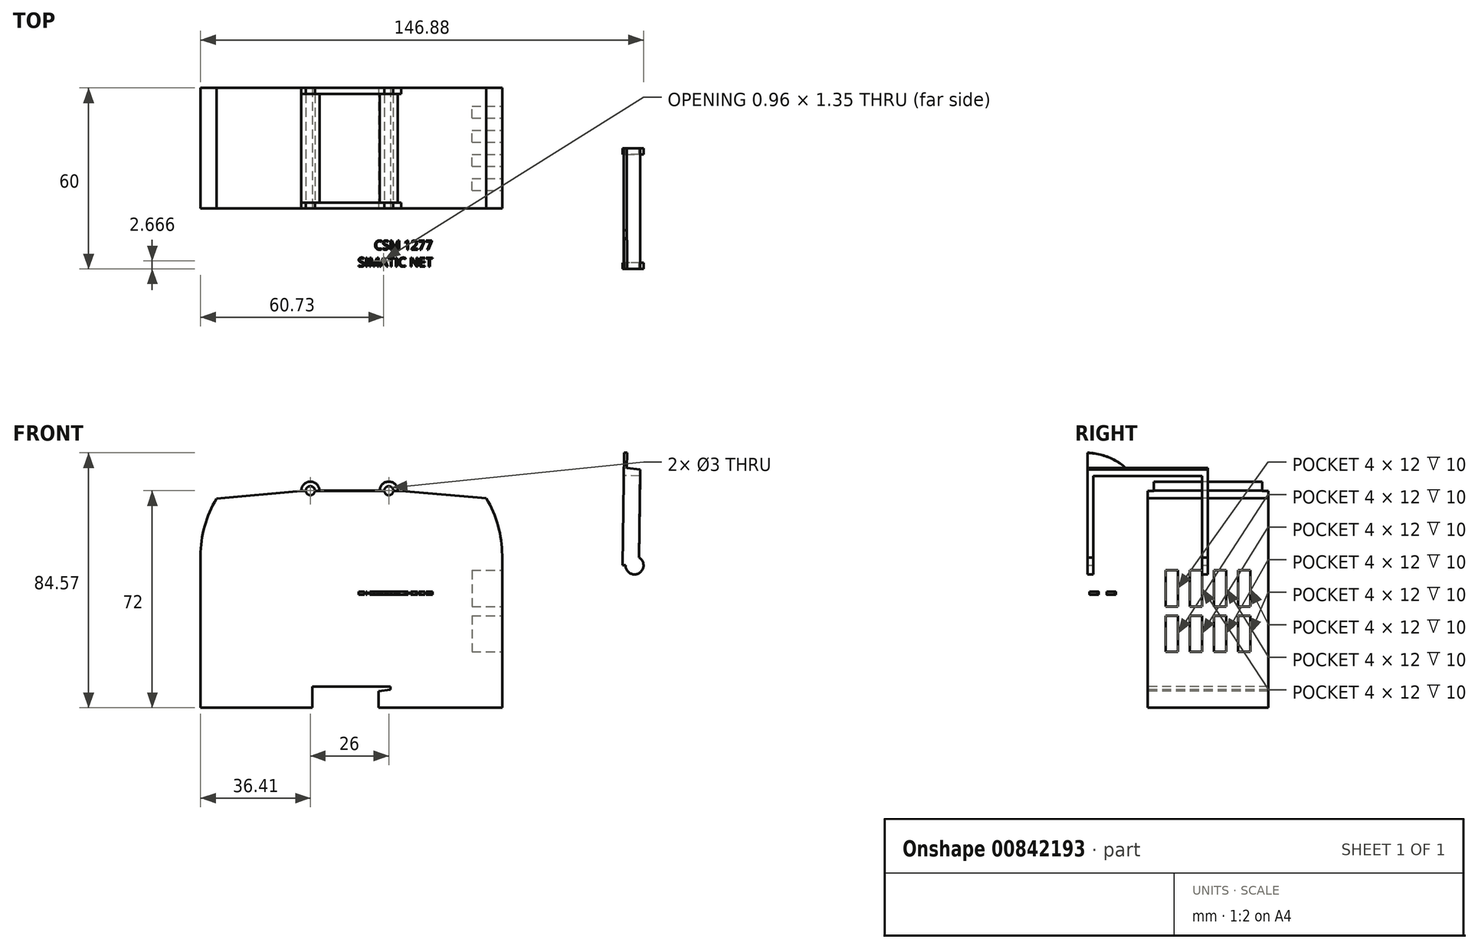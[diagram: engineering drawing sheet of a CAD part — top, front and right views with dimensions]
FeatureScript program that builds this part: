
annotation { "Feature Type Name" : "Feature", "Feature Type Description" : "" }
export const myFeature = defineFeature(function(context is Context, id is Id, definition is map)
    precondition{}
    {
        {
            var Q0;
            Q0=qCreatedBy(makeId("Front.planeOp"),FACE);
            var sketch = newSketch(context, id + "F0", { "sketchPlane" : qUnion([Q0])});
            skLineSegment(sketch, "E0.bottom", {"start": v(50, -37.5) * mm, "end": v(-50, -37.5) * mm});
            skLineSegment(sketch, "E0.top", {"start": v(50, 37.5) * mm, "end": v(-50, 37.5) * mm});
            skLineSegment(sketch, "E0.left", {"start": v(50, -37.5) * mm, "end": v(50, 37.5) * mm});
            skLineSegment(sketch, "E0.right", {"start": v(-50, -37.5) * mm, "end": v(-50, 37.5) * mm});
            skPoint(sketch, "E0.middle", {"position": v(0, 0) * mm});
            skSolve(sketch);
        }
        {
            var Q0;
            Q0=makeQuery(id+"F0.imprint","IMPRINT",FACE,{"disambiguationData":[TD([[makeQuery(id+"F0.imprint","IMPRINT",EDGE,{"derivedFrom":sQuery(id+"F0.wireOp",EDGE,"E0.bottom")}),-1.0]])]});
            extrude(context, id + "F1", {"entities" : qUnion([Q0]), "endBound" : BoundingType.SYMMETRIC, "depth" : 40 * mm, "offsetDistance" : 25 * mm});
        }
        {
            var Q0;
            Q0=makeQuery(id+"F1.opExtrude","CAP_FACE",FACE,{"disambiguationData":[OSD([sQuery(id+"F0.wireOp",EDGE,"E0.bottom"),sQuery(id+"F0.wireOp",EDGE,"E0.top"),sQuery(id+"F0.wireOp",EDGE,"E0.left"),sQuery(id+"F0.wireOp",EDGE,"E0.right")])],"isStart":false});
            var sketch = newSketch(context, id + "F2", { "sketchPlane" : qUnion([Q0])});
            skCircle(sketch, "E1", {"center": v(12.41, 34.5) * mm, "radius": 3 * mm});
            skCircle(sketch, "E2", {"center": v(-13.59, 34.5) * mm, "radius": 3 * mm});
            skLineSegment(sketch, "E3", {"start": v(9.41, 34.5) * mm, "end": v(15.41, 34.5) * mm});
            skLineSegment(sketch, "E4", {"start": v(-10.59, 34.5) * mm, "end": v(-16.59, 34.5) * mm});
            skLineSegment(sketch, "E5", {"start": v(15.41, 34.5) * mm, "end": v(50, 31.5) * mm});
            skLineSegment(sketch, "E6.MirrorCS", {"start": v(-15.09, 34.5) * mm, "end": v(-50.09, 31.36) * mm});
            skLineSegment(sketch, "E7", {"start": v(-10.59, 34.5) * mm, "end": v(9.41, 34.5) * mm});
            skCircle(sketch, "E8", {"center": v(-13.59, 34.5) * mm, "radius": 1.5 * mm});
            skCircle(sketch, "E9", {"center": v(12.41, 34.5) * mm, "radius": 1.5 * mm});
            skLineSegment(sketch, "E10", {"start": v(-50.09, 31.36) * mm, "end": v(-50, 37.5) * mm});
            skLineSegment(sketch, "E11", {"start": v(-50, 37.5) * mm, "end": v(50, 37.5) * mm});
            skLineSegment(sketch, "E12", {"start": v(50, 37.5) * mm, "end": v(50, 31.5) * mm});
            skSolve(sketch);
        }
        {
            var Q0;
            {var subQ3=sQuery(id+"F2.wireOp",EDGE,"E2");var subQ8=makeQuery(id+"F2.imprint","INTERSECT",VERTEX,{"derivedFrom":[subQ3,sQuery(id+"F2.wireOp",EDGE,"E4")]});Q0=makeQuery(id+"F2.imprint","IMPRINT",FACE,{"disambiguationData":[TD([[makeQuery(id+"F2.imprint","IMPRINT",EDGE,{"disambiguationData":[TD([[subQ8,1.0]])],"derivedFrom":subQ3}),-1.0]])]});}
            var Q1;
            {var subQ0=sQuery(id+"F2.wireOp",EDGE,"E7");Q1=makeQuery(id+"F2.imprint","IMPRINT",FACE,{"disambiguationData":[TD([[makeQuery(id+"F2.imprint","IMPRINT",EDGE,{"derivedFrom":subQ0}),1.0]])]});}
            var Q2;
            {var subQ0=sQuery(id+"F2.wireOp",EDGE,"E5");Q2=makeQuery(id+"F2.imprint","IMPRINT",FACE,{"disambiguationData":[TD([[makeQuery(id+"F2.imprint","IMPRINT",EDGE,{"derivedFrom":subQ0}),1.0]])]});}
            var Q3;
            {var subQ0=sQuery(id+"F2.wireOp",EDGE,"E8");var subQ1=sQuery(id+"F2.wireOp",EDGE,"E4");var subQ3=makeQuery(id+"F2.imprint","INTERSECT",VERTEX,{"derivedFrom":[subQ1,subQ0]});Q3=makeQuery(id+"F2.imprint","IMPRINT",FACE,{"disambiguationData":[TD([[makeQuery(id+"F2.imprint","IMPRINT",EDGE,{"disambiguationData":[TD([[subQ3,-1.0]])],"derivedFrom":subQ1}),-1.0]])]});}
            var Q4;
            {var subQ0=sQuery(id+"F2.wireOp",EDGE,"E8");var subQ1=sQuery(id+"F2.wireOp",EDGE,"E4");var subQ3=makeQuery(id+"F2.imprint","INTERSECT",VERTEX,{"derivedFrom":[subQ1,subQ0]});Q4=makeQuery(id+"F2.imprint","IMPRINT",FACE,{"disambiguationData":[TD([[makeQuery(id+"F2.imprint","IMPRINT",EDGE,{"disambiguationData":[TD([[subQ3,-1.0]])],"derivedFrom":subQ1}),1.0]])]});}
            var Q5;
            {var subQ0=sQuery(id+"F2.wireOp",EDGE,"E9");var subQ1=sQuery(id+"F2.wireOp",EDGE,"E3");var subQ2=makeQuery(id+"F2.imprint","INTERSECT",VERTEX,{"disambiguationData":[OD(0.0)],"derivedFrom":[subQ1,subQ0]});Q5=makeQuery(id+"F2.imprint","IMPRINT",FACE,{"disambiguationData":[TD([[makeQuery(id+"F2.imprint","IMPRINT",EDGE,{"disambiguationData":[TD([[subQ2,-1.0]])],"derivedFrom":subQ1}),1.0]])]});}
            var Q6;
            {var subQ0=sQuery(id+"F2.wireOp",EDGE,"E9");var subQ1=sQuery(id+"F2.wireOp",EDGE,"E3");var subQ2=makeQuery(id+"F2.imprint","INTERSECT",VERTEX,{"disambiguationData":[OD(0.0)],"derivedFrom":[subQ1,subQ0]});Q6=makeQuery(id+"F2.imprint","IMPRINT",FACE,{"disambiguationData":[TD([[makeQuery(id+"F2.imprint","IMPRINT",EDGE,{"disambiguationData":[TD([[subQ2,-1.0]])],"derivedFrom":subQ1}),-1.0]])]});}
            extrude(context, id + "F3", {"entities" : qUnion([Q0, Q1, Q2, Q3, Q4, Q5, Q6]), "operationType" : NewBodyOperationType.REMOVE, "oppositeDirection" : true, "depth" : 40 * mm, "offsetDistance" : 25 * mm});
        }
        {
            var Q0;
            Q0=makeQuery(id+"F1.opExtrude","CAP_FACE",FACE,{"disambiguationData":[OSD([sQuery(id+"F0.wireOp",EDGE,"E0.bottom"),sQuery(id+"F0.wireOp",EDGE,"E0.top"),sQuery(id+"F0.wireOp",EDGE,"E0.left"),sQuery(id+"F0.wireOp",EDGE,"E0.right")])],"isStart":false});
            var sketch = newSketch(context, id + "F4", { "sketchPlane" : qUnion([Q0])});
            skArc(sketch, "E13", {"start": v(-44.71, 31.84) * mm, "mid": v(-48.66, 22.65) * mm, "end": v(-50, 12.74) * mm});
            skArc(sketch, "E14", {"start": v(50, 12.74) * mm, "mid": v(48.68, 22.71) * mm, "end": v(44.71, 31.96) * mm});
            skSolve(sketch);
        }
        {
            var Q0;
            {var subQ0=sQuery(id+"F4.wireOp",EDGE,"E13");var subQ1=makeQuery(id+"F3.boolean.opBoolean","COPY",EDGE,{"derivedFrom":makeQuery(id+"F3.opExtrude","CAP_EDGE",EDGE,{"disambiguationData":[OSD([sQuery(id+"F2.wireOp",EDGE,"E6.MirrorCS")])],"isStart":true})});var subQ2=makeQuery(id+"F4.imprint","INTERSECT",VERTEX,{"derivedFrom":[subQ1,subQ0]});Q0=makeQuery(id+"F4.imprint","IMPRINT",FACE,{"disambiguationData":[TD([[makeQuery(id+"F4.imprint","IMPRINT",EDGE,{"disambiguationData":[TD([[subQ2,-1.0]])],"derivedFrom":subQ0}),-1.0]])]});}
            var Q1;
            {var subQ0=sQuery(id+"F4.wireOp",EDGE,"E14");var subQ1=makeQuery(id+"F3.boolean.opBoolean","COPY",EDGE,{"derivedFrom":makeQuery(id+"F3.opExtrude","CAP_EDGE",EDGE,{"disambiguationData":[OSD([sQuery(id+"F2.wireOp",EDGE,"E5")])],"isStart":true})});var subQ2=makeQuery(id+"F4.imprint","INTERSECT",VERTEX,{"derivedFrom":[subQ1,subQ0]});Q1=makeQuery(id+"F4.imprint","IMPRINT",FACE,{"disambiguationData":[TD([[makeQuery(id+"F4.imprint","IMPRINT",EDGE,{"disambiguationData":[TD([[subQ2,1.0]])],"derivedFrom":subQ0}),-1.0]])]});}
            extrude(context, id + "F5", {"entities" : qUnion([Q0, Q1]), "operationType" : NewBodyOperationType.REMOVE, "oppositeDirection" : true, "depth" : 40 * mm, "offsetDistance" : 25 * mm});
        }
        {
            var Q0;
            Q0=makeQuery(id+"F1.opExtrude","SWEPT_FACE",FACE,{"disambiguationData":[OSD([sQuery(id+"F0.wireOp",EDGE,"E0.left")])]});
            var sketch = newSketch(context, id + "F6", { "sketchPlane" : qUnion([Q0])});
            skLineSegment(sketch, "E15.bottom", {"start": v(-14, 8.06) * mm, "end": v(-10, 8.06) * mm});
            skLineSegment(sketch, "E15.top", {"start": v(-14, -3.94) * mm, "end": v(-10, -3.94) * mm});
            skLineSegment(sketch, "E15.left", {"start": v(-14, 8.06) * mm, "end": v(-14, -3.94) * mm});
            skLineSegment(sketch, "E15.right", {"start": v(-10, 8.06) * mm, "end": v(-10, -3.94) * mm});
            skLineSegment(sketch, "E16.0.1.0", {"start": v(-14, -6.94) * mm, "end": v(-10, -6.94) * mm});
            skLineSegment(sketch, "E16.0.1.1", {"start": v(-10, -6.94) * mm, "end": v(-10, -18.94) * mm});
            skLineSegment(sketch, "E16.0.1.2", {"start": v(-14, -6.94) * mm, "end": v(-14, -18.94) * mm});
            skLineSegment(sketch, "E16.0.1.3", {"start": v(-14, -18.94) * mm, "end": v(-10, -18.94) * mm});
            skLineSegment(sketch, "E16.1.0.0", {"start": v(-6, 8.06) * mm, "end": v(-2, 8.06) * mm});
            skLineSegment(sketch, "E16.1.0.1", {"start": v(-2, 8.06) * mm, "end": v(-2, -3.94) * mm});
            skLineSegment(sketch, "E16.1.0.2", {"start": v(-6, 8.06) * mm, "end": v(-6, -3.94) * mm});
            skLineSegment(sketch, "E16.1.0.3", {"start": v(-6, -3.94) * mm, "end": v(-2, -3.94) * mm});
            skLineSegment(sketch, "E16.1.1.0", {"start": v(-6, -6.94) * mm, "end": v(-2, -6.94) * mm});
            skLineSegment(sketch, "E16.1.1.1", {"start": v(-2, -6.94) * mm, "end": v(-2, -18.94) * mm});
            skLineSegment(sketch, "E16.1.1.2", {"start": v(-6, -6.94) * mm, "end": v(-6, -18.94) * mm});
            skLineSegment(sketch, "E16.1.1.3", {"start": v(-6, -18.94) * mm, "end": v(-2, -18.94) * mm});
            skLineSegment(sketch, "E16.2.0.0", {"start": v(2, 8.06) * mm, "end": v(6, 8.06) * mm});
            skLineSegment(sketch, "E16.2.0.1", {"start": v(6, 8.06) * mm, "end": v(6, -3.94) * mm});
            skLineSegment(sketch, "E16.2.0.2", {"start": v(2, 8.06) * mm, "end": v(2, -3.94) * mm});
            skLineSegment(sketch, "E16.2.0.3", {"start": v(2, -3.94) * mm, "end": v(6, -3.94) * mm});
            skLineSegment(sketch, "E16.2.1.0", {"start": v(2, -6.94) * mm, "end": v(6, -6.94) * mm});
            skLineSegment(sketch, "E16.2.1.1", {"start": v(6, -6.94) * mm, "end": v(6, -18.94) * mm});
            skLineSegment(sketch, "E16.2.1.2", {"start": v(2, -6.94) * mm, "end": v(2, -18.94) * mm});
            skLineSegment(sketch, "E16.2.1.3", {"start": v(2, -18.94) * mm, "end": v(6, -18.94) * mm});
            skLineSegment(sketch, "E16.3.0.0", {"start": v(10, 8.06) * mm, "end": v(14, 8.06) * mm});
            skLineSegment(sketch, "E16.3.0.1", {"start": v(14, 8.06) * mm, "end": v(14, -3.94) * mm});
            skLineSegment(sketch, "E16.3.0.2", {"start": v(10, 8.06) * mm, "end": v(10, -3.94) * mm});
            skLineSegment(sketch, "E16.3.0.3", {"start": v(10, -3.94) * mm, "end": v(14, -3.94) * mm});
            skLineSegment(sketch, "E16.3.1.0", {"start": v(10, -6.94) * mm, "end": v(14, -6.94) * mm});
            skLineSegment(sketch, "E16.3.1.1", {"start": v(14, -6.94) * mm, "end": v(14, -18.94) * mm});
            skLineSegment(sketch, "E16.3.1.2", {"start": v(10, -6.94) * mm, "end": v(10, -18.94) * mm});
            skLineSegment(sketch, "E16.3.1.3", {"start": v(10, -18.94) * mm, "end": v(14, -18.94) * mm});
            skLineSegment(sketch, "E16.direction1", {"start": v(-14, 8.06) * mm, "end": v(-6, 8.06) * mm, "construction": true});
            skLineSegment(sketch, "E16.direction2", {"start": v(-14, 8.06) * mm, "end": v(-14, -6.94) * mm, "construction": true});
            skSolve(sketch);
        }
        {
            var Q0;
            Q0=makeQuery(id+"F6.imprint","IMPRINT",FACE,{"disambiguationData":[TD([[makeQuery(id+"F6.imprint","IMPRINT",EDGE,{"derivedFrom":sQuery(id+"F6.wireOp",EDGE,"E15.bottom")}),-1.0]])]});
            var Q1;
            Q1=makeQuery(id+"F6.imprint","IMPRINT",FACE,{"disambiguationData":[TD([[makeQuery(id+"F6.imprint","IMPRINT",EDGE,{"derivedFrom":sQuery(id+"F6.wireOp",EDGE,"E16.1.0.0")}),-1.0]])]});
            var Q2;
            Q2=makeQuery(id+"F6.imprint","IMPRINT",FACE,{"disambiguationData":[TD([[makeQuery(id+"F6.imprint","IMPRINT",EDGE,{"derivedFrom":sQuery(id+"F6.wireOp",EDGE,"E16.2.0.0")}),-1.0]])]});
            var Q3;
            Q3=makeQuery(id+"F6.imprint","IMPRINT",FACE,{"disambiguationData":[TD([[makeQuery(id+"F6.imprint","IMPRINT",EDGE,{"derivedFrom":sQuery(id+"F6.wireOp",EDGE,"E16.3.0.0")}),-1.0]])]});
            var Q4;
            Q4=makeQuery(id+"F6.imprint","IMPRINT",FACE,{"disambiguationData":[TD([[makeQuery(id+"F6.imprint","IMPRINT",EDGE,{"derivedFrom":sQuery(id+"F6.wireOp",EDGE,"E16.3.1.0")}),-1.0]])]});
            var Q5;
            Q5=makeQuery(id+"F6.imprint","IMPRINT",FACE,{"disambiguationData":[TD([[makeQuery(id+"F6.imprint","IMPRINT",EDGE,{"derivedFrom":sQuery(id+"F6.wireOp",EDGE,"E16.2.1.0")}),-1.0]])]});
            var Q6;
            Q6=makeQuery(id+"F6.imprint","IMPRINT",FACE,{"disambiguationData":[TD([[makeQuery(id+"F6.imprint","IMPRINT",EDGE,{"derivedFrom":sQuery(id+"F6.wireOp",EDGE,"E16.1.1.0")}),-1.0]])]});
            var Q7;
            Q7=makeQuery(id+"F6.imprint","IMPRINT",FACE,{"disambiguationData":[TD([[makeQuery(id+"F6.imprint","IMPRINT",EDGE,{"derivedFrom":sQuery(id+"F6.wireOp",EDGE,"E16.0.1.0")}),-1.0]])]});
            extrude(context, id + "F7", {"entities" : qUnion([Q0, Q1, Q2, Q3, Q4, Q5, Q6, Q7]), "operationType" : NewBodyOperationType.REMOVE, "oppositeDirection" : true, "depth" : 10 * mm, "offsetDistance" : 25 * mm});
        }
        {
            var Q0;
            Q0=makeQuery(id+"F1.opExtrude","SWEPT_FACE",FACE,{"disambiguationData":[OSD([sQuery(id+"F0.wireOp",EDGE,"E0.right")])]});
            var sketch = newSketch(context, id + "F8", { "sketchPlane" : qUnion([Q0])});
            skLineSegment(sketch, "E17", {"start": v(-20.02, 34.4) * mm, "end": v(-18.02, 34.4) * mm});
            skLineSegment(sketch, "E18", {"start": v(-18.02, 34.4) * mm, "end": v(-18.02, 38.84) * mm});
            skLineSegment(sketch, "E19", {"start": v(-18.02, 38.84) * mm, "end": v(-20.02, 38.84) * mm});
            skLineSegment(sketch, "E20", {"start": v(-20.02, 38.84) * mm, "end": v(-20.02, 34.4) * mm});
            skLineSegment(sketch, "E21.MirrorCS", {"start": v(18.02, 34.4) * mm, "end": v(18.02, 38.84) * mm});
            skLineSegment(sketch, "E22.MirrorCS", {"start": v(18.02, 38.84) * mm, "end": v(20.02, 38.84) * mm});
            skLineSegment(sketch, "E23.MirrorCS", {"start": v(20.02, 38.84) * mm, "end": v(20.02, 34.4) * mm});
            skLineSegment(sketch, "E24.MirrorCS", {"start": v(20.02, 34.4) * mm, "end": v(18.02, 34.4) * mm});
            skSolve(sketch);
        }
        {
            var Q0;
            Q0=makeQuery(id+"F8.imprint","IMPRINT",FACE,{"disambiguationData":[TD([[makeQuery(id+"F8.imprint","IMPRINT",EDGE,{"derivedFrom":sQuery(id+"F8.wireOp",EDGE,"E17")}),1.0]])]});
            var Q1;
            Q1=makeQuery(id+"F8.imprint","IMPRINT",FACE,{"disambiguationData":[TD([[makeQuery(id+"F8.imprint","IMPRINT",EDGE,{"derivedFrom":sQuery(id+"F8.wireOp",EDGE,"E21.MirrorCS")}),-1.0]])]});
            extrude(context, id + "F9", {"entities" : qUnion([Q0, Q1]), "operationType" : NewBodyOperationType.REMOVE, "oppositeDirection" : true, "depth" : 100 * mm, "offsetDistance" : 25 * mm});
        }
        {
            var Q0;
            Q0=qCreatedBy(makeId("Top.planeOp"),FACE);
            var sketch = newSketch(context, id + "F10", { "sketchPlane" : qUnion([Q0])});
            skText(sketch, "E25", { "text": "     CSM 1277\nSIMATIC NET", "fontName": "OpenSans-Regular.ttf"});
            const initialGuessF10  = {"E25": [0.0022, -0.0336, 1, 0, 0.003]};
            skSetInitialGuess(sketch, initialGuessF10);
            skSolve(sketch);
        }
        {
            var Q0;
            Q0 = qSketchRegion(id + "F10", true);
            extrude(context, id + "F11", {"entities" : qUnion([Q0]), "depth" : 1 * mm, "offsetDistance" : 25 * mm});
        }
        {
            var Q0;
            Q0=qCreatedBy(makeId("Front.planeOp"),FACE);
            var sketch = newSketch(context, id + "F12", { "sketchPlane" : qUnion([Q0])});
            skLineSegment(sketch, "E26", {"start": v(95.79, 41.48) * mm, "end": v(95.44, 12.24) * mm});
            skLineSegment(sketch, "E27", {"start": v(91.35, 42.05) * mm, "end": v(95.79, 41.48) * mm});
            skCircle(sketch, "E28", {"center": v(93.88, 9.72) * mm, "radius": 3 * mm});
            skLineSegment(sketch, "E29", {"start": v(90.88, 9.76) * mm, "end": v(91.35, 42.05) * mm});
            skSolve(sketch);
        }
        {
            var Q0;
            {var subQ0=sQuery(id+"F12.wireOp",EDGE,"E27");Q0=makeQuery(id+"F12.imprint","IMPRINT",FACE,{"disambiguationData":[TD([[makeQuery(id+"F12.imprint","IMPRINT",EDGE,{"derivedFrom":subQ0}),-1.0]])]});}
            var Q1;
            {var subQ0=sQuery(id+"F12.wireOp",EDGE,"E28");var subQ1=makeQuery(id+"F12.imprint","INTERSECT",VERTEX,{"derivedFrom":[subQ0,sQuery(id+"F12.wireOp",EDGE,"E29")]});Q1=makeQuery(id+"F12.imprint","IMPRINT",FACE,{"disambiguationData":[TD([[makeQuery(id+"F12.imprint","IMPRINT",EDGE,{"disambiguationData":[TD([[subQ1,1.0]])],"derivedFrom":subQ0}),1.0]])]});}
            extrude(context, id + "F13", {"entities" : qUnion([Q0, Q1]), "depth" : 40 * mm, "offsetDistance" : 25 * mm});
        }
        {
            var Q0;
            Q0=makeQuery(id+"F13.opExtrude","SWEPT_FACE",FACE,{"disambiguationData":[OSD([sQuery(id+"F12.wireOp",EDGE,"E29")])]});
            var sketch = newSketch(context, id + "F14", { "sketchPlane" : qUnion([Q0])});
            skLineSegment(sketch, "E30", {"start": v(40, 11.08) * mm, "end": v(40, 43.37) * mm});
            skLineSegment(sketch, "E31", {"start": v(40, 43.37) * mm, "end": v(0, 43.37) * mm});
            skLineSegment(sketch, "E32", {"start": v(0, 43.37) * mm, "end": v(0, 5.8) * mm});
            skLineSegment(sketch, "E33", {"start": v(0, 5.8) * mm, "end": v(2, 5.8) * mm});
            skLineSegment(sketch, "E34", {"start": v(2, 5.8) * mm, "end": v(2, 40.76) * mm});
            skLineSegment(sketch, "E35", {"start": v(2, 40.76) * mm, "end": v(38, 40.76) * mm});
            skLineSegment(sketch, "E36", {"start": v(38, 40.76) * mm, "end": v(38, 5.4) * mm});
            skLineSegment(sketch, "E37", {"start": v(38, 5.4) * mm, "end": v(40, 5.4) * mm});
            skLineSegment(sketch, "E38", {"start": v(40, 5.4) * mm, "end": v(40, 11.08) * mm});
            skLineSegment(sketch, "E39", {"start": v(38, 5.4) * mm, "end": v(2, 5.8) * mm});
            skSolve(sketch);
        }
        {
            var Q0;
            {var subQ0=sQuery(id+"F14.wireOp",EDGE,"E35");Q0=makeQuery(id+"F14.imprint","IMPRINT",FACE,{"disambiguationData":[TD([[makeQuery(id+"F14.imprint","IMPRINT",EDGE,{"derivedFrom":subQ0}),-1.0]])]});}
            var Q1;
            {var subQ0=sQuery(id+"F14.wireOp",EDGE,"E39");Q1=makeQuery(id+"F14.imprint","IMPRINT",FACE,{"disambiguationData":[TD([[makeQuery(id+"F14.imprint","IMPRINT",EDGE,{"derivedFrom":subQ0}),-1.0]])]});}
            extrude(context, id + "F15", {"entities" : qUnion([Q0, Q1]), "operationType" : NewBodyOperationType.REMOVE, "oppositeDirection" : true, "depth" : 25 * mm, "offsetDistance" : 25 * mm});
        }
        {
            var Q0;
            Q0=makeQuery(id+"F13.opExtrude","SWEPT_FACE",FACE,{"disambiguationData":[OSD([sQuery(id+"F12.wireOp",EDGE,"E29")])]});
            var sketch = newSketch(context, id + "F16", { "sketchPlane" : qUnion([Q0])});
            skLineSegment(sketch, "E40", {"start": v(40, 11.08) * mm, "end": v(40, 43.37) * mm});
            skLineSegment(sketch, "E41", {"start": v(40, 43.37) * mm, "end": v(0, 43.37) * mm});
            skLineSegment(sketch, "E42", {"start": v(0, 43.37) * mm, "end": v(0, 11.08) * mm});
            skLineSegment(sketch, "E43", {"start": v(0, 11.08) * mm, "end": v(40, 11.08) * mm});
            skLineSegment(sketch, "E44", {"start": v(40, 43.37) * mm, "end": v(40, 48.37) * mm});
            skArc(sketch, "E45", {"start": v(40, 48.37) * mm, "mid": v(33.2, 46.96) * mm, "end": v(27.24, 43.37) * mm});
            skSolve(sketch);
        }
        {
            var Q0;
            {var subQ1=makeQuery(id+"F15.boolean.opBoolean","COPY",EDGE,{"derivedFrom":makeQuery(id+"F15.opExtrude","CAP_EDGE",EDGE,{"disambiguationData":[OSD([sQuery(id+"F14.wireOp",EDGE,"E34")])],"isStart":true})});Q0=makeQuery(id+"F16.imprint","IMPRINT",FACE,{"disambiguationData":[TD([[makeQuery(id+"F16.imprint","IMPRINT",EDGE,{"derivedFrom":subQ1}),-1.0]])]});}
            var Q1;
            {var subQ1=sQuery(id+"F16.wireOp",EDGE,"E40");Q1=makeQuery(id+"F16.imprint","IMPRINT",FACE,{"disambiguationData":[TD([[makeQuery(id+"F16.imprint","IMPRINT",EDGE,{"derivedFrom":subQ1}),1.0]])]});}
            var Q2;
            {var subQ0=sQuery(id+"F16.wireOp",EDGE,"E44");Q2=makeQuery(id+"F16.imprint","IMPRINT",FACE,{"disambiguationData":[TD([[makeQuery(id+"F16.imprint","IMPRINT",EDGE,{"derivedFrom":subQ0}),1.0]])]});}
            extrude(context, id + "F17", {"entities" : qUnion([Q0, Q1, Q2]), "operationType" : NewBodyOperationType.ADD, "depth" : 1 * mm, "offsetDistance" : 25 * mm});
        }
        {
            var Q0;
            Q0=makeQuery(id+"F1.opExtrude","CAP_FACE",FACE,{"disambiguationData":[OSD([sQuery(id+"F0.wireOp",EDGE,"E0.bottom"),sQuery(id+"F0.wireOp",EDGE,"E0.top"),sQuery(id+"F0.wireOp",EDGE,"E0.left"),sQuery(id+"F0.wireOp",EDGE,"E0.right")])],"isStart":false});
            var sketch = newSketch(context, id + "F18", { "sketchPlane" : qUnion([Q0])});
            skLineSegment(sketch, "E46", {"start": v(0, -30.5) * mm, "end": v(-13, -30.5) * mm});
            skLineSegment(sketch, "E47", {"start": v(-13, -30.5) * mm, "end": v(13, -30.5) * mm});
            skLineSegment(sketch, "E48", {"start": v(13, -30.5) * mm, "end": v(13, -37.5) * mm});
            skLineSegment(sketch, "E49", {"start": v(13, -37.5) * mm, "end": v(-13, -37.5) * mm});
            skLineSegment(sketch, "E50", {"start": v(-13, -37.5) * mm, "end": v(-13, -30.5) * mm});
            skLineSegment(sketch, "E51", {"start": v(13, -30.5) * mm, "end": v(13, -31.5) * mm});
            skLineSegment(sketch, "E52", {"start": v(13, -31.5) * mm, "end": v(9, -32) * mm});
            skLineSegment(sketch, "E53", {"start": v(9, -32) * mm, "end": v(9, -37.5) * mm});
            skSolve(sketch);
        }
        {
            var Q0;
            {var subQ0=sQuery(id+"F18.wireOp",EDGE,"E50");Q0=makeQuery(id+"F18.imprint","IMPRINT",FACE,{"disambiguationData":[TD([[makeQuery(id+"F18.imprint","IMPRINT",EDGE,{"derivedFrom":subQ0}),-1.0]])]});}
            extrude(context, id + "F19", {"entities" : qUnion([Q0]), "operationType" : NewBodyOperationType.REMOVE, "oppositeDirection" : true, "depth" : 43.8 * mm, "offsetDistance" : 25 * mm});
        }
    });
